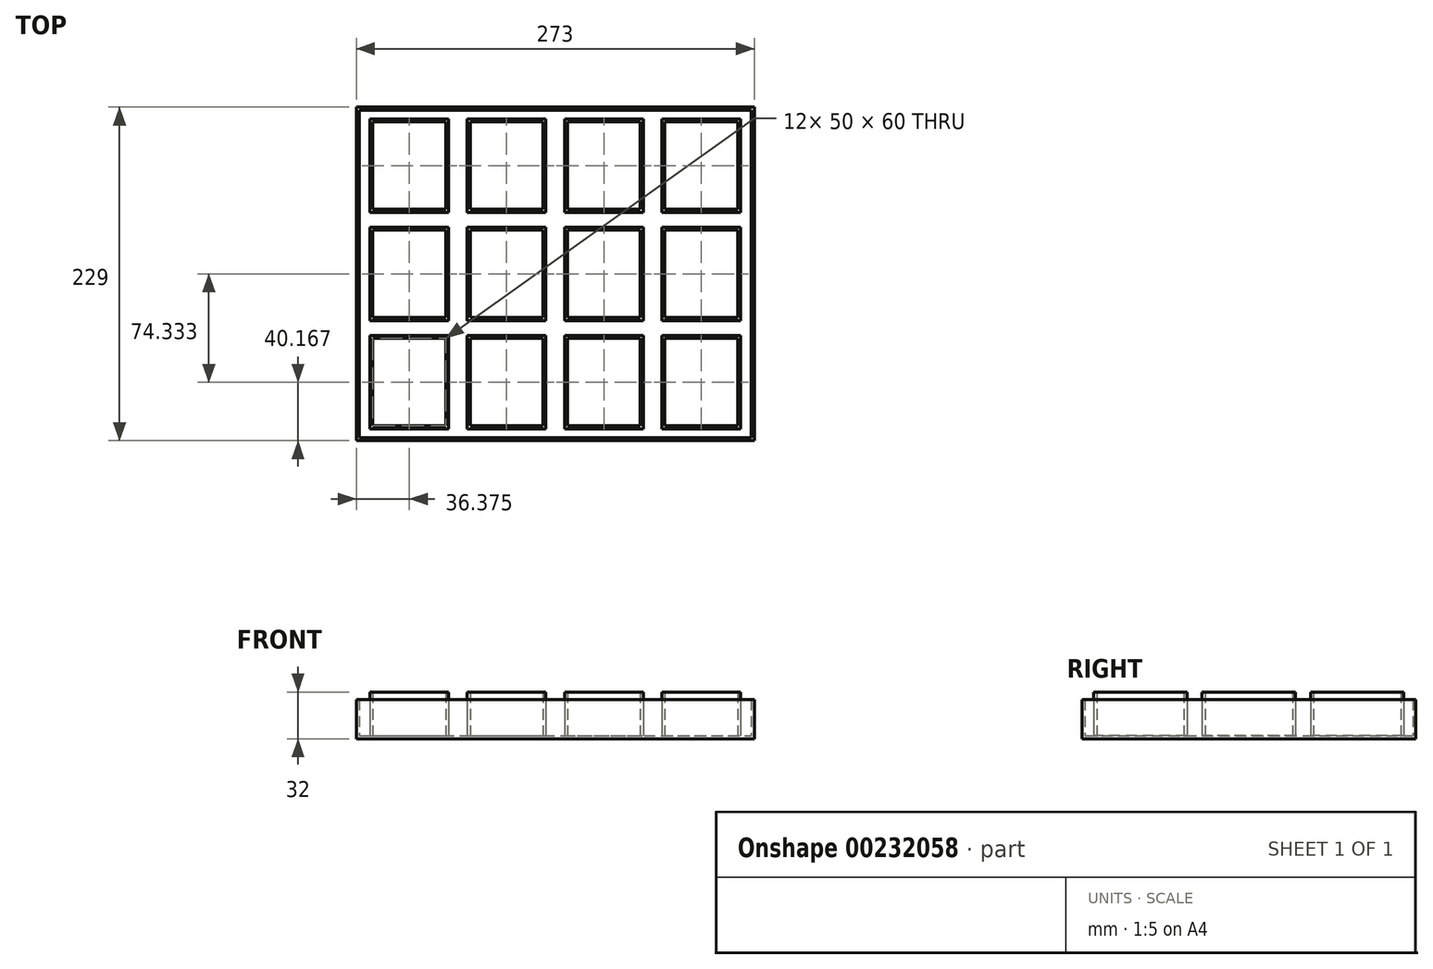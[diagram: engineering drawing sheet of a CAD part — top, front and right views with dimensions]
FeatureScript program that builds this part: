
annotation { "Feature Type Name" : "Feature", "Feature Type Description" : "" }
export const myFeature = defineFeature(function(context is Context, id is Id, definition is map)
    precondition{}
    {
        {
            var Q0;
            Q0=qCreatedBy(makeId("Top.planeOp"),FACE);
            var sketch = newSketch(context, id + "F0", { "sketchPlane" : qUnion([Q0])});
            skLineSegment(sketch, "E0.bottom", {"start": v(0, 0) * mm, "end": v(267, 0) * mm, "construction": true});
            skLineSegment(sketch, "E0.top", {"start": v(0, 223) * mm, "end": v(267, 223) * mm, "construction": true});
            skLineSegment(sketch, "E0.left", {"start": v(0, 0) * mm, "end": v(0, 223) * mm, "construction": true});
            skLineSegment(sketch, "E0.right", {"start": v(267, 0) * mm, "end": v(267, 223) * mm, "construction": true});
            skLineSegment(sketch, "E1.0", {"start": v(-3, -3) * mm, "end": v(-3, 226) * mm});
            skLineSegment(sketch, "E1.1", {"start": v(-3, -3) * mm, "end": v(270, -3) * mm});
            skLineSegment(sketch, "E1.2", {"start": v(270, -3) * mm, "end": v(270, 226) * mm});
            skLineSegment(sketch, "E1.3", {"start": v(-3, 226) * mm, "end": v(270, 226) * mm});
            skLineSegment(sketch, "E2", {"start": v(66.75, 0) * mm, "end": v(66.75, 223) * mm, "construction": true});
            skLineSegment(sketch, "E3", {"start": v(133.5, 223) * mm, "end": v(133.5, 0) * mm, "construction": true});
            skLineSegment(sketch, "E4", {"start": v(200.25, 223) * mm, "end": v(200.25, 0) * mm, "construction": true});
            skLineSegment(sketch, "E5", {"start": v(0, 148.67) * mm, "end": v(267, 148.67) * mm, "construction": true});
            skLineSegment(sketch, "E6", {"start": v(0, 74.33) * mm, "end": v(267, 74.33) * mm, "construction": true});
            skLineSegment(sketch, "E7", {"start": v(0, 148.67) * mm, "end": v(66.75, 223) * mm, "construction": true});
            skLineSegment(sketch, "E8.bottom", {"start": v(8.37, 215.83) * mm, "end": v(58.37, 215.83) * mm});
            skLineSegment(sketch, "E8.top", {"start": v(8.37, 155.83) * mm, "end": v(58.37, 155.83) * mm});
            skLineSegment(sketch, "E8.left", {"start": v(8.37, 215.83) * mm, "end": v(8.37, 155.83) * mm});
            skLineSegment(sketch, "E8.right", {"start": v(58.37, 215.83) * mm, "end": v(58.37, 155.83) * mm});
            skPoint(sketch, "E8.middle", {"position": v(33.37, 185.83) * mm});
            skLineSegment(sketch, "E9.0.1.0", {"start": v(8.37, 141.5) * mm, "end": v(58.37, 141.5) * mm});
            skLineSegment(sketch, "E9.0.1.1", {"start": v(8.38, 141.5) * mm, "end": v(8.38, 81.5) * mm});
            skLineSegment(sketch, "E9.0.1.2", {"start": v(58.37, 141.5) * mm, "end": v(58.37, 81.5) * mm});
            skLineSegment(sketch, "E9.0.1.3", {"start": v(8.37, 81.5) * mm, "end": v(58.37, 81.5) * mm});
            skLineSegment(sketch, "E9.0.1.4", {"start": v(133.5, 148.67) * mm, "end": v(133.5, -74.33) * mm, "construction": true});
            skLineSegment(sketch, "E9.0.2.0", {"start": v(8.37, 67.17) * mm, "end": v(58.37, 67.17) * mm});
            skLineSegment(sketch, "E9.0.2.1", {"start": v(8.38, 67.17) * mm, "end": v(8.38, 7.17) * mm});
            skLineSegment(sketch, "E9.0.2.2", {"start": v(58.37, 67.17) * mm, "end": v(58.37, 7.17) * mm});
            skLineSegment(sketch, "E9.0.2.3", {"start": v(8.37, 7.17) * mm, "end": v(58.37, 7.17) * mm});
            skLineSegment(sketch, "E9.0.2.4", {"start": v(133.5, 74.33) * mm, "end": v(133.5, -148.67) * mm, "construction": true});
            skLineSegment(sketch, "E9.1.0.0", {"start": v(75.12, 215.83) * mm, "end": v(125.12, 215.83) * mm});
            skLineSegment(sketch, "E9.1.0.1", {"start": v(75.12, 215.83) * mm, "end": v(75.12, 155.83) * mm});
            skLineSegment(sketch, "E9.1.0.2", {"start": v(125.12, 215.83) * mm, "end": v(125.12, 155.83) * mm});
            skLineSegment(sketch, "E9.1.0.3", {"start": v(75.12, 155.83) * mm, "end": v(125.12, 155.83) * mm});
            skLineSegment(sketch, "E9.1.1.0", {"start": v(75.12, 141.5) * mm, "end": v(125.12, 141.5) * mm});
            skLineSegment(sketch, "E9.1.1.1", {"start": v(75.12, 141.5) * mm, "end": v(75.12, 81.5) * mm});
            skLineSegment(sketch, "E9.1.1.2", {"start": v(125.12, 141.5) * mm, "end": v(125.12, 81.5) * mm});
            skLineSegment(sketch, "E9.1.1.3", {"start": v(75.12, 81.5) * mm, "end": v(125.12, 81.5) * mm});
            skLineSegment(sketch, "E9.1.1.4", {"start": v(200.25, 148.67) * mm, "end": v(200.25, -74.33) * mm, "construction": true});
            skLineSegment(sketch, "E9.1.2.0", {"start": v(75.12, 67.17) * mm, "end": v(125.12, 67.17) * mm});
            skLineSegment(sketch, "E9.1.2.1", {"start": v(75.12, 67.17) * mm, "end": v(75.12, 7.17) * mm});
            skLineSegment(sketch, "E9.1.2.2", {"start": v(125.12, 67.17) * mm, "end": v(125.12, 7.17) * mm});
            skLineSegment(sketch, "E9.1.2.3", {"start": v(75.12, 7.17) * mm, "end": v(125.12, 7.17) * mm});
            skLineSegment(sketch, "E9.1.2.4", {"start": v(200.25, 74.33) * mm, "end": v(200.25, -148.67) * mm, "construction": true});
            skLineSegment(sketch, "E9.2.0.0", {"start": v(141.87, 215.83) * mm, "end": v(191.87, 215.83) * mm});
            skLineSegment(sketch, "E9.2.0.1", {"start": v(141.87, 215.83) * mm, "end": v(141.87, 155.83) * mm});
            skLineSegment(sketch, "E9.2.0.2", {"start": v(191.87, 215.83) * mm, "end": v(191.87, 155.83) * mm});
            skLineSegment(sketch, "E9.2.0.3", {"start": v(141.87, 155.83) * mm, "end": v(191.87, 155.83) * mm});
            skLineSegment(sketch, "E9.2.0.4", {"start": v(267, 223) * mm, "end": v(267, 0) * mm, "construction": true});
            skLineSegment(sketch, "E9.2.1.0", {"start": v(141.87, 141.5) * mm, "end": v(191.87, 141.5) * mm});
            skLineSegment(sketch, "E9.2.1.1", {"start": v(141.87, 141.5) * mm, "end": v(141.87, 81.5) * mm});
            skLineSegment(sketch, "E9.2.1.2", {"start": v(191.87, 141.5) * mm, "end": v(191.87, 81.5) * mm});
            skLineSegment(sketch, "E9.2.1.3", {"start": v(141.87, 81.5) * mm, "end": v(191.87, 81.5) * mm});
            skLineSegment(sketch, "E9.2.1.4", {"start": v(267, 148.67) * mm, "end": v(267, -74.33) * mm, "construction": true});
            skLineSegment(sketch, "E9.2.2.0", {"start": v(141.87, 67.17) * mm, "end": v(191.87, 67.17) * mm});
            skLineSegment(sketch, "E9.2.2.1", {"start": v(141.87, 67.17) * mm, "end": v(141.87, 7.17) * mm});
            skLineSegment(sketch, "E9.2.2.2", {"start": v(191.87, 67.17) * mm, "end": v(191.87, 7.17) * mm});
            skLineSegment(sketch, "E9.2.2.3", {"start": v(141.87, 7.17) * mm, "end": v(191.87, 7.17) * mm});
            skLineSegment(sketch, "E9.2.2.4", {"start": v(267, 74.33) * mm, "end": v(267, -148.67) * mm, "construction": true});
            skLineSegment(sketch, "E9.3.0.0", {"start": v(208.62, 215.83) * mm, "end": v(258.62, 215.83) * mm});
            skLineSegment(sketch, "E9.3.0.1", {"start": v(208.62, 215.83) * mm, "end": v(208.62, 155.83) * mm});
            skLineSegment(sketch, "E9.3.0.2", {"start": v(258.62, 215.83) * mm, "end": v(258.62, 155.83) * mm});
            skLineSegment(sketch, "E9.3.0.3", {"start": v(208.62, 155.83) * mm, "end": v(258.62, 155.83) * mm});
            skLineSegment(sketch, "E9.3.0.4", {"start": v(333.75, 223) * mm, "end": v(333.75, 0) * mm, "construction": true});
            skLineSegment(sketch, "E9.3.1.0", {"start": v(208.62, 141.5) * mm, "end": v(258.62, 141.5) * mm});
            skLineSegment(sketch, "E9.3.1.1", {"start": v(208.62, 141.5) * mm, "end": v(208.62, 81.5) * mm});
            skLineSegment(sketch, "E9.3.1.2", {"start": v(258.62, 141.5) * mm, "end": v(258.62, 81.5) * mm});
            skLineSegment(sketch, "E9.3.1.3", {"start": v(208.62, 81.5) * mm, "end": v(258.62, 81.5) * mm});
            skLineSegment(sketch, "E9.3.1.4", {"start": v(333.75, 148.67) * mm, "end": v(333.75, -74.33) * mm, "construction": true});
            skLineSegment(sketch, "E9.3.2.0", {"start": v(208.62, 67.17) * mm, "end": v(258.62, 67.17) * mm});
            skLineSegment(sketch, "E9.3.2.1", {"start": v(208.62, 67.17) * mm, "end": v(208.62, 7.17) * mm});
            skLineSegment(sketch, "E9.3.2.2", {"start": v(258.62, 67.17) * mm, "end": v(258.62, 7.17) * mm});
            skLineSegment(sketch, "E9.3.2.3", {"start": v(208.62, 7.17) * mm, "end": v(258.62, 7.17) * mm});
            skLineSegment(sketch, "E9.3.2.4", {"start": v(333.75, 74.33) * mm, "end": v(333.75, -148.67) * mm, "construction": true});
            skLineSegment(sketch, "E9.direction1", {"start": v(8.37, 155.83) * mm, "end": v(75.12, 155.83) * mm, "construction": true});
            skLineSegment(sketch, "E9.direction2", {"start": v(8.37, 155.83) * mm, "end": v(8.37, 81.5) * mm, "construction": true});
            skSolve(sketch);
        }
        {
            var Q0;
            Q0 = qSketchRegion(id + "F0", true);
            extrude(context, id + "F1", {"entities" : qUnion([Q0]), "depth" : 2 * mm});
        }
        {
            var Q0;
            Q0=makeQuery(id+"F1.opExtrude","CAP_FACE",FACE,{"disambiguationData":[OSD([sQuery(id+"F0.wireOp",EDGE,"E1.0"),sQuery(id+"F0.wireOp",EDGE,"E1.1"),sQuery(id+"F0.wireOp",EDGE,"E1.2"),sQuery(id+"F0.wireOp",EDGE,"E1.3"),sQuery(id+"F0.wireOp",EDGE,"E8.bottom"),sQuery(id+"F0.wireOp",EDGE,"E8.top"),sQuery(id+"F0.wireOp",EDGE,"E8.left"),sQuery(id+"F0.wireOp",EDGE,"E8.right"),sQuery(id+"F0.wireOp",EDGE,"E9.0.1.0"),sQuery(id+"F0.wireOp",EDGE,"E9.0.1.1"),sQuery(id+"F0.wireOp",EDGE,"E9.0.1.2"),sQuery(id+"F0.wireOp",EDGE,"E9.0.1.3"),sQuery(id+"F0.wireOp",EDGE,"E9.0.2.0"),sQuery(id+"F0.wireOp",EDGE,"E9.0.2.1"),sQuery(id+"F0.wireOp",EDGE,"E9.0.2.2"),sQuery(id+"F0.wireOp",EDGE,"E9.0.2.3"),sQuery(id+"F0.wireOp",EDGE,"E9.1.0.0"),sQuery(id+"F0.wireOp",EDGE,"E9.1.0.1"),sQuery(id+"F0.wireOp",EDGE,"E9.1.0.2"),sQuery(id+"F0.wireOp",EDGE,"E9.1.0.3"),sQuery(id+"F0.wireOp",EDGE,"E9.1.1.0"),sQuery(id+"F0.wireOp",EDGE,"E9.1.1.1"),sQuery(id+"F0.wireOp",EDGE,"E9.1.1.2"),sQuery(id+"F0.wireOp",EDGE,"E9.1.1.3"),sQuery(id+"F0.wireOp",EDGE,"E9.1.2.0"),sQuery(id+"F0.wireOp",EDGE,"E9.1.2.1"),sQuery(id+"F0.wireOp",EDGE,"E9.1.2.2"),sQuery(id+"F0.wireOp",EDGE,"E9.1.2.3"),sQuery(id+"F0.wireOp",EDGE,"E9.2.0.0"),sQuery(id+"F0.wireOp",EDGE,"E9.2.0.1"),sQuery(id+"F0.wireOp",EDGE,"E9.2.0.2"),sQuery(id+"F0.wireOp",EDGE,"E9.2.0.3"),sQuery(id+"F0.wireOp",EDGE,"E9.2.1.0"),sQuery(id+"F0.wireOp",EDGE,"E9.2.1.1"),sQuery(id+"F0.wireOp",EDGE,"E9.2.1.2"),sQuery(id+"F0.wireOp",EDGE,"E9.2.1.3"),sQuery(id+"F0.wireOp",EDGE,"E9.2.2.0"),sQuery(id+"F0.wireOp",EDGE,"E9.2.2.1"),sQuery(id+"F0.wireOp",EDGE,"E9.2.2.2"),sQuery(id+"F0.wireOp",EDGE,"E9.2.2.3"),sQuery(id+"F0.wireOp",EDGE,"E9.3.0.0"),sQuery(id+"F0.wireOp",EDGE,"E9.3.0.1"),sQuery(id+"F0.wireOp",EDGE,"E9.3.0.2"),sQuery(id+"F0.wireOp",EDGE,"E9.3.0.3"),sQuery(id+"F0.wireOp",EDGE,"E9.3.1.0"),sQuery(id+"F0.wireOp",EDGE,"E9.3.1.1"),sQuery(id+"F0.wireOp",EDGE,"E9.3.1.2"),sQuery(id+"F0.wireOp",EDGE,"E9.3.1.3"),sQuery(id+"F0.wireOp",EDGE,"E9.3.2.0"),sQuery(id+"F0.wireOp",EDGE,"E9.3.2.1"),sQuery(id+"F0.wireOp",EDGE,"E9.3.2.2"),sQuery(id+"F0.wireOp",EDGE,"E9.3.2.3")])],"isStart":false});
            var sketch = newSketch(context, id + "F2", { "sketchPlane" : qUnion([Q0])});
            skLineSegment(sketch, "E10.0", {"start": v(-3, -3) * mm, "end": v(-3, 226) * mm});
            skLineSegment(sketch, "E10.1", {"start": v(-3, 226) * mm, "end": v(270, 226) * mm});
            skLineSegment(sketch, "E10.2", {"start": v(270, -3) * mm, "end": v(270, 226) * mm});
            skLineSegment(sketch, "E10.3", {"start": v(-3, -3) * mm, "end": v(270, -3) * mm});
            skLineSegment(sketch, "E11.0", {"start": v(-1, -1) * mm, "end": v(-1, 224) * mm});
            skLineSegment(sketch, "E11.1", {"start": v(-1, -1) * mm, "end": v(268, -1) * mm});
            skLineSegment(sketch, "E11.2", {"start": v(268, -1) * mm, "end": v(268, 224) * mm});
            skLineSegment(sketch, "E11.3", {"start": v(-1, 224) * mm, "end": v(268, 224) * mm});
            skSolve(sketch);
        }
        {
            var Q0;
            Q0 = qSketchRegion(id + "F2", true);
            extrude(context, id + "F3", {"entities" : qUnion([Q0]), "operationType" : NewBodyOperationType.ADD, "depth" : 25 * mm});
        }
        {
            var Q0;
            Q0=makeQuery(id+"F1.opExtrude","CAP_FACE",FACE,{"disambiguationData":[OSD([sQuery(id+"F0.wireOp",EDGE,"E1.0"),sQuery(id+"F0.wireOp",EDGE,"E1.1"),sQuery(id+"F0.wireOp",EDGE,"E1.2"),sQuery(id+"F0.wireOp",EDGE,"E1.3"),sQuery(id+"F0.wireOp",EDGE,"E8.bottom"),sQuery(id+"F0.wireOp",EDGE,"E8.top"),sQuery(id+"F0.wireOp",EDGE,"E8.left"),sQuery(id+"F0.wireOp",EDGE,"E8.right"),sQuery(id+"F0.wireOp",EDGE,"E9.0.1.0"),sQuery(id+"F0.wireOp",EDGE,"E9.0.1.1"),sQuery(id+"F0.wireOp",EDGE,"E9.0.1.2"),sQuery(id+"F0.wireOp",EDGE,"E9.0.1.3"),sQuery(id+"F0.wireOp",EDGE,"E9.0.2.0"),sQuery(id+"F0.wireOp",EDGE,"E9.0.2.1"),sQuery(id+"F0.wireOp",EDGE,"E9.0.2.2"),sQuery(id+"F0.wireOp",EDGE,"E9.0.2.3"),sQuery(id+"F0.wireOp",EDGE,"E9.1.0.0"),sQuery(id+"F0.wireOp",EDGE,"E9.1.0.1"),sQuery(id+"F0.wireOp",EDGE,"E9.1.0.2"),sQuery(id+"F0.wireOp",EDGE,"E9.1.0.3"),sQuery(id+"F0.wireOp",EDGE,"E9.1.1.0"),sQuery(id+"F0.wireOp",EDGE,"E9.1.1.1"),sQuery(id+"F0.wireOp",EDGE,"E9.1.1.2"),sQuery(id+"F0.wireOp",EDGE,"E9.1.1.3"),sQuery(id+"F0.wireOp",EDGE,"E9.1.2.0"),sQuery(id+"F0.wireOp",EDGE,"E9.1.2.1"),sQuery(id+"F0.wireOp",EDGE,"E9.1.2.2"),sQuery(id+"F0.wireOp",EDGE,"E9.1.2.3"),sQuery(id+"F0.wireOp",EDGE,"E9.2.0.0"),sQuery(id+"F0.wireOp",EDGE,"E9.2.0.1"),sQuery(id+"F0.wireOp",EDGE,"E9.2.0.2"),sQuery(id+"F0.wireOp",EDGE,"E9.2.0.3"),sQuery(id+"F0.wireOp",EDGE,"E9.2.1.0"),sQuery(id+"F0.wireOp",EDGE,"E9.2.1.1"),sQuery(id+"F0.wireOp",EDGE,"E9.2.1.2"),sQuery(id+"F0.wireOp",EDGE,"E9.2.1.3"),sQuery(id+"F0.wireOp",EDGE,"E9.2.2.0"),sQuery(id+"F0.wireOp",EDGE,"E9.2.2.1"),sQuery(id+"F0.wireOp",EDGE,"E9.2.2.2"),sQuery(id+"F0.wireOp",EDGE,"E9.2.2.3"),sQuery(id+"F0.wireOp",EDGE,"E9.3.0.0"),sQuery(id+"F0.wireOp",EDGE,"E9.3.0.1"),sQuery(id+"F0.wireOp",EDGE,"E9.3.0.2"),sQuery(id+"F0.wireOp",EDGE,"E9.3.0.3"),sQuery(id+"F0.wireOp",EDGE,"E9.3.1.0"),sQuery(id+"F0.wireOp",EDGE,"E9.3.1.1"),sQuery(id+"F0.wireOp",EDGE,"E9.3.1.2"),sQuery(id+"F0.wireOp",EDGE,"E9.3.1.3"),sQuery(id+"F0.wireOp",EDGE,"E9.3.2.0"),sQuery(id+"F0.wireOp",EDGE,"E9.3.2.1"),sQuery(id+"F0.wireOp",EDGE,"E9.3.2.2"),sQuery(id+"F0.wireOp",EDGE,"E9.3.2.3")])],"isStart":false});
            var sketch = newSketch(context, id + "F4", { "sketchPlane" : qUnion([Q0])});
            skLineSegment(sketch, "E12.0", {"start": v(8.37, 215.83) * mm, "end": v(8.37, 155.83) * mm});
            skLineSegment(sketch, "E12.1", {"start": v(8.37, 215.83) * mm, "end": v(58.37, 215.83) * mm});
            skLineSegment(sketch, "E12.2", {"start": v(58.37, 215.83) * mm, "end": v(58.37, 155.83) * mm});
            skLineSegment(sketch, "E12.3", {"start": v(8.37, 155.83) * mm, "end": v(58.37, 155.83) * mm});
            skLineSegment(sketch, "E13.0", {"start": v(6.37, 153.83) * mm, "end": v(60.37, 153.83) * mm});
            skLineSegment(sketch, "E13.1", {"start": v(6.37, 217.83) * mm, "end": v(6.37, 153.83) * mm});
            skLineSegment(sketch, "E13.2", {"start": v(6.37, 217.83) * mm, "end": v(60.37, 217.83) * mm});
            skLineSegment(sketch, "E13.3", {"start": v(60.37, 217.83) * mm, "end": v(60.37, 153.83) * mm});
            skLineSegment(sketch, "E14.0.1.0", {"start": v(60.37, 143.5) * mm, "end": v(60.37, 79.5) * mm});
            skLineSegment(sketch, "E14.0.1.1", {"start": v(6.37, 143.5) * mm, "end": v(60.37, 143.5) * mm});
            skLineSegment(sketch, "E14.0.1.2", {"start": v(6.37, 143.5) * mm, "end": v(6.37, 79.5) * mm});
            skLineSegment(sketch, "E14.0.1.3", {"start": v(6.37, 79.5) * mm, "end": v(60.37, 79.5) * mm});
            skLineSegment(sketch, "E14.0.1.4", {"start": v(8.37, 81.5) * mm, "end": v(58.37, 81.5) * mm});
            skLineSegment(sketch, "E14.0.1.5", {"start": v(58.37, 141.5) * mm, "end": v(58.37, 81.5) * mm});
            skLineSegment(sketch, "E14.0.1.6", {"start": v(8.37, 141.5) * mm, "end": v(58.37, 141.5) * mm});
            skLineSegment(sketch, "E14.0.1.7", {"start": v(8.37, 141.5) * mm, "end": v(8.37, 81.5) * mm});
            skLineSegment(sketch, "E14.0.2.0", {"start": v(60.37, 69.17) * mm, "end": v(60.37, 5.17) * mm});
            skLineSegment(sketch, "E14.0.2.1", {"start": v(6.37, 69.17) * mm, "end": v(60.37, 69.17) * mm});
            skLineSegment(sketch, "E14.0.2.2", {"start": v(6.37, 69.17) * mm, "end": v(6.37, 5.17) * mm});
            skLineSegment(sketch, "E14.0.2.3", {"start": v(6.37, 5.17) * mm, "end": v(60.37, 5.17) * mm});
            skLineSegment(sketch, "E14.0.2.4", {"start": v(8.37, 7.17) * mm, "end": v(58.37, 7.17) * mm});
            skLineSegment(sketch, "E14.0.2.5", {"start": v(58.37, 67.17) * mm, "end": v(58.37, 7.17) * mm});
            skLineSegment(sketch, "E14.0.2.6", {"start": v(8.37, 67.17) * mm, "end": v(58.37, 67.17) * mm});
            skLineSegment(sketch, "E14.0.2.7", {"start": v(8.37, 67.17) * mm, "end": v(8.37, 7.17) * mm});
            skLineSegment(sketch, "E14.1.0.0", {"start": v(127.12, 217.83) * mm, "end": v(127.12, 153.83) * mm});
            skLineSegment(sketch, "E14.1.0.1", {"start": v(73.12, 217.83) * mm, "end": v(127.12, 217.83) * mm});
            skLineSegment(sketch, "E14.1.0.2", {"start": v(73.12, 217.83) * mm, "end": v(73.12, 153.83) * mm});
            skLineSegment(sketch, "E14.1.0.3", {"start": v(73.12, 153.83) * mm, "end": v(127.12, 153.83) * mm});
            skLineSegment(sketch, "E14.1.0.4", {"start": v(75.12, 155.83) * mm, "end": v(125.12, 155.83) * mm});
            skLineSegment(sketch, "E14.1.0.5", {"start": v(125.12, 215.83) * mm, "end": v(125.12, 155.83) * mm});
            skLineSegment(sketch, "E14.1.0.6", {"start": v(75.12, 215.83) * mm, "end": v(125.12, 215.83) * mm});
            skLineSegment(sketch, "E14.1.0.7", {"start": v(75.12, 215.83) * mm, "end": v(75.12, 155.83) * mm});
            skLineSegment(sketch, "E14.1.1.0", {"start": v(127.12, 143.5) * mm, "end": v(127.12, 79.5) * mm});
            skLineSegment(sketch, "E14.1.1.1", {"start": v(73.12, 143.5) * mm, "end": v(127.12, 143.5) * mm});
            skLineSegment(sketch, "E14.1.1.2", {"start": v(73.12, 143.5) * mm, "end": v(73.12, 79.5) * mm});
            skLineSegment(sketch, "E14.1.1.3", {"start": v(73.12, 79.5) * mm, "end": v(127.12, 79.5) * mm});
            skLineSegment(sketch, "E14.1.1.4", {"start": v(75.12, 81.5) * mm, "end": v(125.12, 81.5) * mm});
            skLineSegment(sketch, "E14.1.1.5", {"start": v(125.12, 141.5) * mm, "end": v(125.12, 81.5) * mm});
            skLineSegment(sketch, "E14.1.1.6", {"start": v(75.12, 141.5) * mm, "end": v(125.12, 141.5) * mm});
            skLineSegment(sketch, "E14.1.1.7", {"start": v(75.12, 141.5) * mm, "end": v(75.12, 81.5) * mm});
            skLineSegment(sketch, "E14.1.2.0", {"start": v(127.12, 69.17) * mm, "end": v(127.12, 5.17) * mm});
            skLineSegment(sketch, "E14.1.2.1", {"start": v(73.12, 69.17) * mm, "end": v(127.12, 69.17) * mm});
            skLineSegment(sketch, "E14.1.2.2", {"start": v(73.12, 69.17) * mm, "end": v(73.12, 5.17) * mm});
            skLineSegment(sketch, "E14.1.2.3", {"start": v(73.12, 5.17) * mm, "end": v(127.12, 5.17) * mm});
            skLineSegment(sketch, "E14.1.2.4", {"start": v(75.12, 7.17) * mm, "end": v(125.12, 7.17) * mm});
            skLineSegment(sketch, "E14.1.2.5", {"start": v(125.12, 67.17) * mm, "end": v(125.12, 7.17) * mm});
            skLineSegment(sketch, "E14.1.2.6", {"start": v(75.12, 67.17) * mm, "end": v(125.12, 67.17) * mm});
            skLineSegment(sketch, "E14.1.2.7", {"start": v(75.12, 67.17) * mm, "end": v(75.12, 7.17) * mm});
            skLineSegment(sketch, "E14.2.0.0", {"start": v(193.87, 217.83) * mm, "end": v(193.87, 153.83) * mm});
            skLineSegment(sketch, "E14.2.0.1", {"start": v(139.87, 217.83) * mm, "end": v(193.87, 217.83) * mm});
            skLineSegment(sketch, "E14.2.0.2", {"start": v(139.87, 217.83) * mm, "end": v(139.87, 153.83) * mm});
            skLineSegment(sketch, "E14.2.0.3", {"start": v(139.87, 153.83) * mm, "end": v(193.87, 153.83) * mm});
            skLineSegment(sketch, "E14.2.0.4", {"start": v(141.87, 155.83) * mm, "end": v(191.87, 155.83) * mm});
            skLineSegment(sketch, "E14.2.0.5", {"start": v(191.87, 215.83) * mm, "end": v(191.87, 155.83) * mm});
            skLineSegment(sketch, "E14.2.0.6", {"start": v(141.87, 215.83) * mm, "end": v(191.87, 215.83) * mm});
            skLineSegment(sketch, "E14.2.0.7", {"start": v(141.87, 215.83) * mm, "end": v(141.87, 155.83) * mm});
            skLineSegment(sketch, "E14.2.1.0", {"start": v(193.87, 143.5) * mm, "end": v(193.87, 79.5) * mm});
            skLineSegment(sketch, "E14.2.1.1", {"start": v(139.87, 143.5) * mm, "end": v(193.87, 143.5) * mm});
            skLineSegment(sketch, "E14.2.1.2", {"start": v(139.87, 143.5) * mm, "end": v(139.87, 79.5) * mm});
            skLineSegment(sketch, "E14.2.1.3", {"start": v(139.87, 79.5) * mm, "end": v(193.87, 79.5) * mm});
            skLineSegment(sketch, "E14.2.1.4", {"start": v(141.87, 81.5) * mm, "end": v(191.87, 81.5) * mm});
            skLineSegment(sketch, "E14.2.1.5", {"start": v(191.87, 141.5) * mm, "end": v(191.87, 81.5) * mm});
            skLineSegment(sketch, "E14.2.1.6", {"start": v(141.87, 141.5) * mm, "end": v(191.87, 141.5) * mm});
            skLineSegment(sketch, "E14.2.1.7", {"start": v(141.87, 141.5) * mm, "end": v(141.87, 81.5) * mm});
            skLineSegment(sketch, "E14.2.2.0", {"start": v(193.87, 69.17) * mm, "end": v(193.87, 5.17) * mm});
            skLineSegment(sketch, "E14.2.2.1", {"start": v(139.87, 69.17) * mm, "end": v(193.87, 69.17) * mm});
            skLineSegment(sketch, "E14.2.2.2", {"start": v(139.87, 69.17) * mm, "end": v(139.87, 5.17) * mm});
            skLineSegment(sketch, "E14.2.2.3", {"start": v(139.87, 5.17) * mm, "end": v(193.87, 5.17) * mm});
            skLineSegment(sketch, "E14.2.2.4", {"start": v(141.87, 7.17) * mm, "end": v(191.87, 7.17) * mm});
            skLineSegment(sketch, "E14.2.2.5", {"start": v(191.87, 67.17) * mm, "end": v(191.87, 7.17) * mm});
            skLineSegment(sketch, "E14.2.2.6", {"start": v(141.87, 67.17) * mm, "end": v(191.87, 67.17) * mm});
            skLineSegment(sketch, "E14.2.2.7", {"start": v(141.87, 67.17) * mm, "end": v(141.87, 7.17) * mm});
            skLineSegment(sketch, "E14.3.0.0", {"start": v(260.62, 217.83) * mm, "end": v(260.62, 153.83) * mm});
            skLineSegment(sketch, "E14.3.0.1", {"start": v(206.62, 217.83) * mm, "end": v(260.62, 217.83) * mm});
            skLineSegment(sketch, "E14.3.0.2", {"start": v(206.62, 217.83) * mm, "end": v(206.62, 153.83) * mm});
            skLineSegment(sketch, "E14.3.0.3", {"start": v(206.62, 153.83) * mm, "end": v(260.62, 153.83) * mm});
            skLineSegment(sketch, "E14.3.0.4", {"start": v(208.62, 155.83) * mm, "end": v(258.62, 155.83) * mm});
            skLineSegment(sketch, "E14.3.0.5", {"start": v(258.62, 215.83) * mm, "end": v(258.62, 155.83) * mm});
            skLineSegment(sketch, "E14.3.0.6", {"start": v(208.62, 215.83) * mm, "end": v(258.62, 215.83) * mm});
            skLineSegment(sketch, "E14.3.0.7", {"start": v(208.62, 215.83) * mm, "end": v(208.62, 155.83) * mm});
            skLineSegment(sketch, "E14.3.1.0", {"start": v(260.62, 143.5) * mm, "end": v(260.62, 79.5) * mm});
            skLineSegment(sketch, "E14.3.1.1", {"start": v(206.62, 143.5) * mm, "end": v(260.62, 143.5) * mm});
            skLineSegment(sketch, "E14.3.1.2", {"start": v(206.62, 143.5) * mm, "end": v(206.62, 79.5) * mm});
            skLineSegment(sketch, "E14.3.1.3", {"start": v(206.62, 79.5) * mm, "end": v(260.62, 79.5) * mm});
            skLineSegment(sketch, "E14.3.1.4", {"start": v(208.62, 81.5) * mm, "end": v(258.62, 81.5) * mm});
            skLineSegment(sketch, "E14.3.1.5", {"start": v(258.62, 141.5) * mm, "end": v(258.62, 81.5) * mm});
            skLineSegment(sketch, "E14.3.1.6", {"start": v(208.62, 141.5) * mm, "end": v(258.62, 141.5) * mm});
            skLineSegment(sketch, "E14.3.1.7", {"start": v(208.62, 141.5) * mm, "end": v(208.62, 81.5) * mm});
            skLineSegment(sketch, "E14.3.2.0", {"start": v(260.62, 69.17) * mm, "end": v(260.62, 5.17) * mm});
            skLineSegment(sketch, "E14.3.2.1", {"start": v(206.62, 69.17) * mm, "end": v(260.62, 69.17) * mm});
            skLineSegment(sketch, "E14.3.2.2", {"start": v(206.62, 69.17) * mm, "end": v(206.62, 5.17) * mm});
            skLineSegment(sketch, "E14.3.2.3", {"start": v(206.62, 5.17) * mm, "end": v(260.62, 5.17) * mm});
            skLineSegment(sketch, "E14.3.2.4", {"start": v(208.62, 7.17) * mm, "end": v(258.62, 7.17) * mm});
            skLineSegment(sketch, "E14.3.2.5", {"start": v(258.62, 67.17) * mm, "end": v(258.62, 7.17) * mm});
            skLineSegment(sketch, "E14.3.2.6", {"start": v(208.62, 67.17) * mm, "end": v(258.62, 67.17) * mm});
            skLineSegment(sketch, "E14.3.2.7", {"start": v(208.62, 67.17) * mm, "end": v(208.62, 7.17) * mm});
            skLineSegment(sketch, "E14.direction1", {"start": v(6.37, 153.83) * mm, "end": v(73.12, 153.83) * mm, "construction": true});
            skLineSegment(sketch, "E14.direction2", {"start": v(6.37, 153.83) * mm, "end": v(6.37, 79.5) * mm, "construction": true});
            skSolve(sketch);
        }
        {
            var Q0;
            Q0 = qSketchRegion(id + "F4", true);
            extrude(context, id + "F5", {"entities" : qUnion([Q0]), "operationType" : NewBodyOperationType.ADD, "depth" : 30 * mm});
        }
    });
